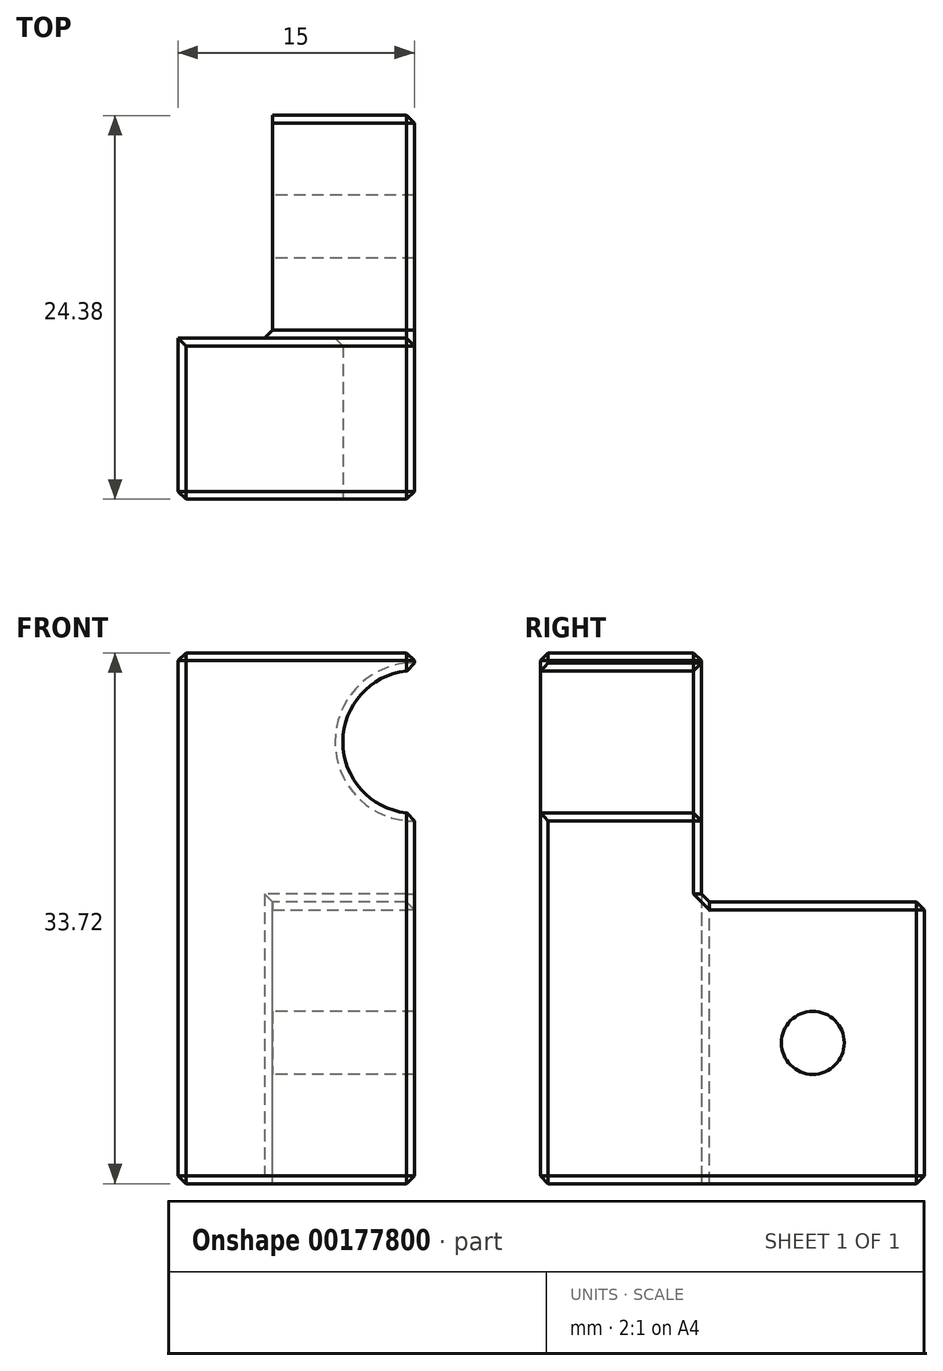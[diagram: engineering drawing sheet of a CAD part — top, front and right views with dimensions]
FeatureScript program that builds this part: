
annotation { "Feature Type Name" : "Feature", "Feature Type Description" : "" }
export const myFeature = defineFeature(function(context is Context, id is Id, definition is map)
    precondition{}
    {
        {
            var Q0;
            Q0=qCreatedBy(makeId("Right.planeOp"),FACE);
            var sketch = newSketch(context, id + "F0", { "sketchPlane" : qUnion([Q0])});
            skLineSegment(sketch, "E0.bottom", {"start": v(0, 0) * mm, "end": v(24.38, 0) * mm});
            skLineSegment(sketch, "E0.top", {"start": v(0, 33.72) * mm, "end": v(10.24, 33.72) * mm});
            skLineSegment(sketch, "E0.left", {"start": v(0, 0) * mm, "end": v(0, 33.72) * mm});
            skLineSegment(sketch, "E0.right", {"start": v(24.38, 0) * mm, "end": v(24.38, 17.89) * mm});
            skLineSegment(sketch, "E1", {"start": v(10.24, 33.72) * mm, "end": v(10.24, 17.89) * mm});
            skLineSegment(sketch, "E2", {"start": v(10.24, 17.89) * mm, "end": v(24.38, 17.89) * mm});
            skSolve(sketch);
        }
        {
            var Q0;
            Q0 = qSketchRegion(id + "F0", true);
            extrude(context, id + "F1", {"entities" : qUnion([Q0]), "depth" : 15 * mm});
        }
        {
            var Q0;
            Q0=makeQuery(id+"F1.opExtrude","SWEPT_FACE",FACE,{"disambiguationData":[OSD([sQuery(id+"F0.wireOp",EDGE,"E0.left")])]});
            var sketch = newSketch(context, id + "F2", { "sketchPlane" : qUnion([Q0])});
            skCircle(sketch, "E3", {"center": v(15, 28.06) * mm, "radius": 4.53 * mm});
            skSolve(sketch);
        }
        {
            var Q0;
            Q0 = qSketchRegion(id + "F2", true);
            extrude(context, id + "F3", {"entities" : qUnion([Q0]), "operationType" : NewBodyOperationType.REMOVE, "oppositeDirection" : true, "depth" : 25 * mm});
        }
        {
            var Q0;
            Q0=makeQuery(id+"F1.opExtrude","CAP_FACE",FACE,{"disambiguationData":[OSD([sQuery(id+"F0.wireOp",EDGE,"E0.bottom"),sQuery(id+"F0.wireOp",EDGE,"E0.top"),sQuery(id+"F0.wireOp",EDGE,"E0.left"),sQuery(id+"F0.wireOp",EDGE,"E0.right"),sQuery(id+"F0.wireOp",EDGE,"E1"),sQuery(id+"F0.wireOp",EDGE,"E2")])],"isStart":true});
            var sketch = newSketch(context, id + "F4", { "sketchPlane" : qUnion([Q0])});
            skLineSegment(sketch, "E4", {"start": v(-10.24, 17.89) * mm, "end": v(-10.24, 0) * mm});
            skSolve(sketch);
        }
        {
            var Q0;
            {var subQ0=sQuery(id+"F4.wireOp",EDGE,"E4");Q0=makeQuery(id+"F4.imprint","IMPRINT",FACE,{"disambiguationData":[TD([[makeQuery(id+"F4.imprint","IMPRINT",EDGE,{"derivedFrom":subQ0}),-1.0]])]});}
            extrude(context, id + "F5", {"entities" : qUnion([Q0]), "operationType" : NewBodyOperationType.REMOVE, "oppositeDirection" : true, "depth" : 6 * mm});
        }
        {
            var Q0;
            Q0=makeQuery(id+"F5.boolean.opBoolean","COPY",FACE,{"derivedFrom":makeQuery(id+"F5.opExtrude","CAP_FACE",FACE,{"disambiguationData":[OSD([sQuery(id+"F0.wireOp",EDGE,"E0.bottom"),sQuery(id+"F0.wireOp",EDGE,"E0.right"),sQuery(id+"F0.wireOp",EDGE,"E2"),sQuery(id+"F4.wireOp",EDGE,"E4")])],"isStart":false})});
            var sketch = newSketch(context, id + "F6", { "sketchPlane" : qUnion([Q0])});
            skPoint(sketch, "E5", {"position": v(-17.31, 8.94) * mm});
            skPoint(sketch, "E5.positionSnap0", {"position": v(-24.38, 8.94) * mm});
            skPoint(sketch, "E5.positionSnap1", {"position": v(-17.31, 17.89) * mm});
            skSolve(sketch);
        }
        {
            var Q0;
            Q0=sQuery(id+"F6.wireOp",VERTEX,"E5");
            var Q1;
            Q1=makeQuery(id+"F1.opExtrude","SWEPT_BODY",BODY,{"disambiguationData":[OSD([sQuery(id+"F0.wireOp",EDGE,"E0.bottom"),sQuery(id+"F0.wireOp",EDGE,"E0.top"),sQuery(id+"F0.wireOp",EDGE,"E0.left"),sQuery(id+"F0.wireOp",EDGE,"E0.right"),sQuery(id+"F0.wireOp",EDGE,"E1"),sQuery(id+"F0.wireOp",EDGE,"E2")])]});
            hole(context, id + "F7", {"style" : HoleStyle.SIMPLE, "endStyle" : HoleEndStyle.THROUGH, "holeDiameter" : 4 * mm, "startFromSketch" : true, "locations" : qUnion([Q0]), "scope" : qUnion([Q1]), "isTappedThrough" : true});
        }
        {
            var Q0;
            Q0=makeQuery(id+"F1.opExtrude","SWEPT_EDGE",EDGE,{"disambiguationData":[OSD([sQuery(id+"F0.wireOp",EDGE,"E0.top"),sQuery(id+"F0.wireOp",EDGE,"E1")])]});
            var Q1;
            Q1=makeQuery(id+"F3.boolean.opBoolean","INTERSECT",EDGE,{"derivedFrom":[makeQuery(id+"F1.opExtrude","SWEPT_FACE",FACE,{"disambiguationData":[OSD([sQuery(id+"F0.wireOp",EDGE,"E1")])]}),makeQuery(id+"F3.opExtrude","SWEPT_FACE",FACE,{"disambiguationData":[OSD([sQuery(id+"F2.wireOp",EDGE,"E3")])]})]});
            var Q2;
            Q2=makeQuery(id+"F1.opExtrude","SWEPT_EDGE",EDGE,{"disambiguationData":[OSD([sQuery(id+"F0.wireOp",EDGE,"E0.top"),sQuery(id+"F0.wireOp",EDGE,"E0.left")])]});
            var Q3;
            Q3=makeQuery(id+"F5.boolean.opBoolean","COPY",EDGE,{"derivedFrom":makeQuery(id+"F5.opExtrude","CAP_EDGE",EDGE,{"disambiguationData":[OSD([sQuery(id+"F0.wireOp",EDGE,"E0.right")])],"isStart":false})});
            var Q4;
            Q4=makeQuery(id+"F1.opExtrude","CAP_EDGE",EDGE,{"disambiguationData":[OSD([sQuery(id+"F0.wireOp",EDGE,"E0.right")])],"isStart":false});
            var Q5;
            Q5=makeQuery(id+"F1.opExtrude","CAP_EDGE",EDGE,{"disambiguationData":[OSD([sQuery(id+"F0.wireOp",EDGE,"E0.bottom")])],"isStart":false});
            var Q6;
            Q6=makeQuery(id+"F3.boolean.opBoolean","COPY",EDGE,{"derivedFrom":makeQuery(id+"F3.opExtrude","CAP_EDGE",EDGE,{"disambiguationData":[OSD([sQuery(id+"F2.wireOp",EDGE,"E3")])],"isStart":true})});
            var Q7;
            Q7=makeQuery(id+"F1.opExtrude","CAP_EDGE",EDGE,{"disambiguationData":[OSD([sQuery(id+"F0.wireOp",EDGE,"E2")])],"isStart":false});
            var Q8;
            {var subQ0=sQuery(id+"F0.wireOp",EDGE,"E0.bottom");var subQ1=sQuery(id+"F0.wireOp",EDGE,"E0.left");Q8=makeQuery(id+"F3.boolean.opBoolean","SPLIT",EDGE,{"disambiguationData":[TD([makeQuery(id+"F1.opExtrude","SWEPT_FACE",FACE,{"disambiguationData":[OSD([subQ0])]})])],"derivedFrom":makeQuery(id+"F1.opExtrude","CAP_EDGE",EDGE,{"disambiguationData":[OSD([subQ1])],"isStart":false})});}
            var Q9;
            {var subQ0=sQuery(id+"F0.wireOp",EDGE,"E1");var subQ1=sQuery(id+"F0.wireOp",EDGE,"E0.right");var subQ2=sQuery(id+"F0.wireOp",EDGE,"E0.left");var subQ3=sQuery(id+"F0.wireOp",EDGE,"E0.bottom");var subQ4=sQuery(id+"F0.wireOp",EDGE,"E2");Q9=makeQuery(id+"F7.hole-0.boolean.opBoolean","INTERSECT",EDGE,{"derivedFrom":[makeQuery(id+"F3.boolean.opBoolean","SPLIT",FACE,{"disambiguationData":[TD([makeQuery(id+"F1.opExtrude","SWEPT_FACE",FACE,{"disambiguationData":[OSD([subQ3])]})])],"derivedFrom":makeQuery(id+"F1.opExtrude","CAP_FACE",FACE,{"disambiguationData":[OSD([subQ3,sQuery(id+"F0.wireOp",EDGE,"E0.top"),subQ2,subQ1,subQ0,subQ4])],"isStart":false})}),makeQuery(id+"F7.hole-0.opRevolve","SWEPT_FACE",FACE,{"disambiguationData":[OSD([sQuery(id+"F7.hole-0.sketch.wireOp",EDGE,"core_line_2")])]})]});}
            var Q10;
            Q10=makeQuery(id+"F1.opExtrude","SWEPT_EDGE",EDGE,{"disambiguationData":[OSD([sQuery(id+"F0.wireOp",EDGE,"E0.bottom"),sQuery(id+"F0.wireOp",EDGE,"E0.right")])]});
            var Q11;
            Q11=makeQuery(id+"F1.opExtrude","SWEPT_EDGE",EDGE,{"disambiguationData":[OSD([sQuery(id+"F0.wireOp",EDGE,"E0.right"),sQuery(id+"F0.wireOp",EDGE,"E2")])]});
            var Q12;
            Q12=makeQuery(id+"F1.opExtrude","SWEPT_EDGE",EDGE,{"disambiguationData":[OSD([sQuery(id+"F0.wireOp",EDGE,"E1"),sQuery(id+"F0.wireOp",EDGE,"E2")])]});
            var Q13;
            Q13=makeQuery(id+"F5.boolean.opBoolean","COPY",EDGE,{"derivedFrom":makeQuery(id+"F5.opExtrude","CAP_EDGE",EDGE,{"disambiguationData":[OSD([sQuery(id+"F0.wireOp",EDGE,"E2")])],"isStart":false})});
            var Q14;
            Q14=makeQuery(id+"F1.opExtrude","SWEPT_EDGE",EDGE,{"disambiguationData":[OSD([sQuery(id+"F0.wireOp",EDGE,"E0.bottom"),sQuery(id+"F0.wireOp",EDGE,"E0.left")])]});
            var Q15;
            Q15=makeQuery(id+"F5.boolean.opBoolean","COPY",EDGE,{"derivedFrom":makeQuery(id+"F5.opExtrude","CAP_EDGE",EDGE,{"disambiguationData":[OSD([sQuery(id+"F4.wireOp",EDGE,"E4")])],"isStart":false})});
            var Q16;
            Q16=makeQuery(id+"F5.boolean.opBoolean","COPY",EDGE,{"derivedFrom":makeQuery(id+"F5.opExtrude","SWEPT_EDGE",EDGE,{"disambiguationData":[OSD([sQuery(id+"F0.wireOp",EDGE,"E0.bottom"),sQuery(id+"F4.wireOp",EDGE,"E4")])]})});
            var Q17;
            Q17=makeQuery(id+"F1.opExtrude","CAP_EDGE",EDGE,{"disambiguationData":[OSD([sQuery(id+"F0.wireOp",EDGE,"E0.top")])],"isStart":true});
            var Q18;
            Q18=makeQuery(id+"F1.opExtrude","CAP_EDGE",EDGE,{"disambiguationData":[OSD([sQuery(id+"F0.wireOp",EDGE,"E0.top")])],"isStart":false});
            var Q19;
            Q19=makeQuery(id+"F1.opExtrude","CAP_EDGE",EDGE,{"disambiguationData":[OSD([sQuery(id+"F0.wireOp",EDGE,"E0.left")])],"isStart":true});
            var Q20;
            Q20=makeQuery(id+"F5.boolean.opBoolean","MERGE",EDGE,{"derivedFrom":[makeQuery(id+"F1.opExtrude","CAP_EDGE",EDGE,{"disambiguationData":[OSD([sQuery(id+"F0.wireOp",EDGE,"E1")])],"isStart":true}),makeQuery(id+"F5.opExtrude","CAP_EDGE",EDGE,{"disambiguationData":[OSD([sQuery(id+"F4.wireOp",EDGE,"E4")])],"isStart":true})]});
            var Q21;
            {var subQ0=sQuery(id+"F0.wireOp",EDGE,"E0.left");var subQ1=sQuery(id+"F0.wireOp",EDGE,"E0.top");Q21=makeQuery(id+"F3.boolean.opBoolean","SPLIT",EDGE,{"disambiguationData":[TD([makeQuery(id+"F1.opExtrude","SWEPT_FACE",FACE,{"disambiguationData":[OSD([subQ1])]})])],"derivedFrom":makeQuery(id+"F1.opExtrude","CAP_EDGE",EDGE,{"disambiguationData":[OSD([subQ0])],"isStart":false})});}
            var Q22;
            {var subQ0=sQuery(id+"F0.wireOp",EDGE,"E1");var subQ1=sQuery(id+"F0.wireOp",EDGE,"E0.top");Q22=makeQuery(id+"F3.boolean.opBoolean","SPLIT",EDGE,{"disambiguationData":[TD([makeQuery(id+"F1.opExtrude","SWEPT_FACE",FACE,{"disambiguationData":[OSD([subQ1])]})])],"derivedFrom":makeQuery(id+"F1.opExtrude","CAP_EDGE",EDGE,{"disambiguationData":[OSD([subQ0])],"isStart":false})});}
            var Q23;
            {var subQ0=sQuery(id+"F0.wireOp",EDGE,"E2");var subQ1=sQuery(id+"F0.wireOp",EDGE,"E1");Q23=makeQuery(id+"F3.boolean.opBoolean","SPLIT",EDGE,{"disambiguationData":[TD([makeQuery(id+"F1.opExtrude","SWEPT_FACE",FACE,{"disambiguationData":[OSD([subQ0])]})])],"derivedFrom":makeQuery(id+"F1.opExtrude","CAP_EDGE",EDGE,{"disambiguationData":[OSD([subQ1])],"isStart":false})});}
            var Q24;
            Q24=makeQuery(id+"F3.boolean.opBoolean","INTERSECT",EDGE,{"disambiguationData":[OD(0.0)],"derivedFrom":[makeQuery(id+"F1.opExtrude","CAP_FACE",FACE,{"disambiguationData":[OSD([sQuery(id+"F0.wireOp",EDGE,"E0.bottom"),sQuery(id+"F0.wireOp",EDGE,"E0.top"),sQuery(id+"F0.wireOp",EDGE,"E0.left"),sQuery(id+"F0.wireOp",EDGE,"E0.right"),sQuery(id+"F0.wireOp",EDGE,"E1"),sQuery(id+"F0.wireOp",EDGE,"E2")])],"isStart":false}),makeQuery(id+"F3.opExtrude","SWEPT_FACE",FACE,{"disambiguationData":[OSD([sQuery(id+"F2.wireOp",EDGE,"E3")])]})]});
            var Q25;
            Q25=makeQuery(id+"F3.boolean.opBoolean","INTERSECT",EDGE,{"disambiguationData":[OD(1.0)],"derivedFrom":[makeQuery(id+"F1.opExtrude","CAP_FACE",FACE,{"disambiguationData":[OSD([sQuery(id+"F0.wireOp",EDGE,"E0.bottom"),sQuery(id+"F0.wireOp",EDGE,"E0.top"),sQuery(id+"F0.wireOp",EDGE,"E0.left"),sQuery(id+"F0.wireOp",EDGE,"E0.right"),sQuery(id+"F0.wireOp",EDGE,"E1"),sQuery(id+"F0.wireOp",EDGE,"E2")])],"isStart":false}),makeQuery(id+"F3.opExtrude","SWEPT_FACE",FACE,{"disambiguationData":[OSD([sQuery(id+"F2.wireOp",EDGE,"E3")])]})]});
            var Q26;
            Q26=makeQuery(id+"F5.boolean.opBoolean","COPY",EDGE,{"derivedFrom":makeQuery(id+"F5.opExtrude","CAP_EDGE",EDGE,{"disambiguationData":[OSD([sQuery(id+"F0.wireOp",EDGE,"E0.bottom")])],"isStart":false})});
            var Q27;
            Q27=makeQuery(id+"F1.opExtrude","CAP_EDGE",EDGE,{"disambiguationData":[OSD([sQuery(id+"F0.wireOp",EDGE,"E0.bottom")])],"isStart":true});
            var Q28;
            Q28=makeQuery(id+"F7.hole-0.boolean.opBoolean","COPY",EDGE,{"derivedFrom":makeQuery(id+"F7.hole-0.opRevolve","SWEPT_EDGE",EDGE,{"disambiguationData":[OSD([sQuery(id+"F7.hole-0.sketch.wireOp",EDGE,"core_line_2"),sQuery(id+"F7.hole-0.sketch.wireOp",EDGE,"core_line_3")])]})});
            chamfer(context, id + "F8", {"entities" : qUnion([Q0, Q1, Q2, Q3, Q4, Q5, Q6, Q7, Q8, Q9, Q10, Q11, Q12, Q13, Q14, Q15, Q16, Q17, Q18, Q19, Q20, Q21, Q22, Q23, Q24, Q25, Q26, Q27, Q28]), "width" : .5 * mm, "tangentPropagation" : true});
        }
    });
